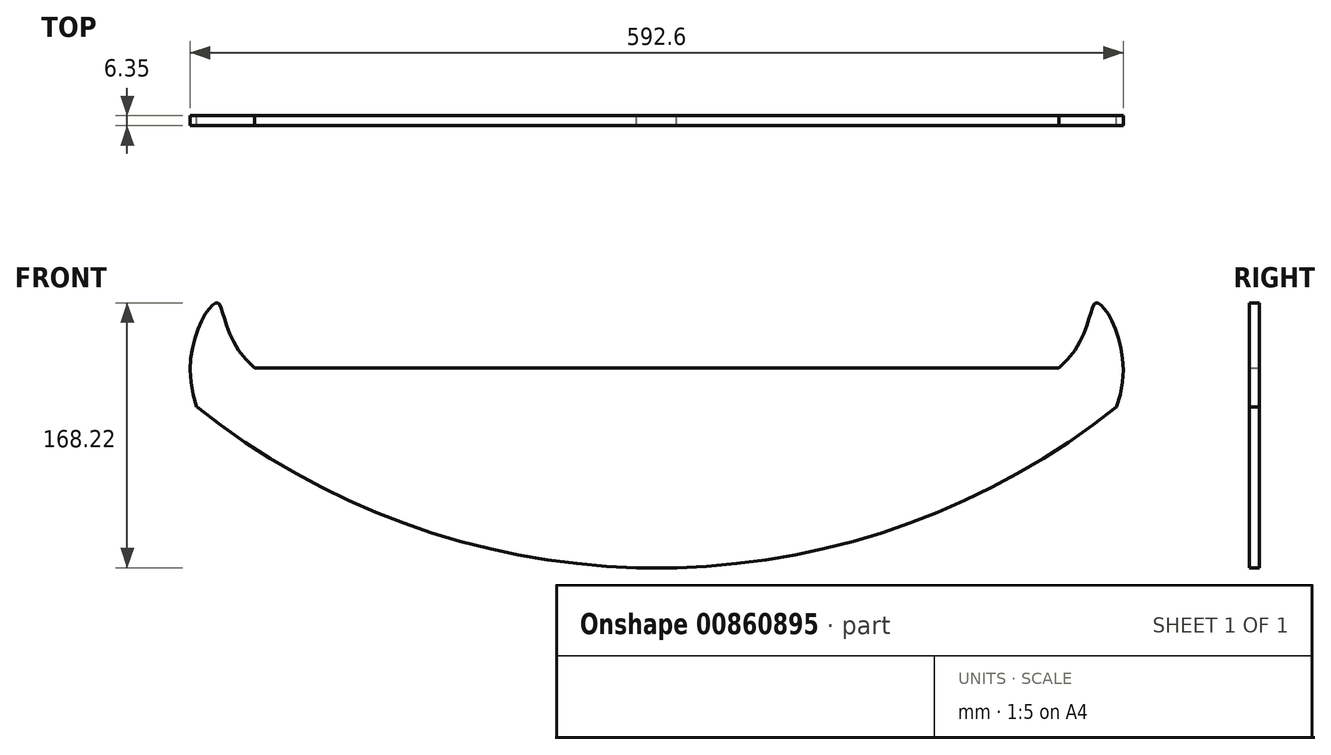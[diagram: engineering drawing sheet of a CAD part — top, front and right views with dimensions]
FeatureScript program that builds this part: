
annotation { "Feature Type Name" : "Feature", "Feature Type Description" : "" }
export const myFeature = defineFeature(function(context is Context, id is Id, definition is map)
    precondition{}
    {
        {
            var Q0;
            Q0=qCreatedBy(makeId("Front.planeOp"),FACE);
            var sketch = newSketch(context, id + "F0", { "sketchPlane" : qUnion([Q0])});
            skPoint(sketch, "E0.MirrorCS.start.orphan", {"position": v(292.1, -12) * mm});
            skPoint(sketch, "E1.MirrorCS.end.orphan", {"position": v(255.56, 12.77) * mm});
            skLineSegment(sketch, "E2", {"start": v(-255.56, 12.77) * mm, "end": v(-12.7, 12.77) * mm});
            skArc(sketch, "E3", {"start": v(-292.1, -12) * mm, "mid": v(-160.74, -85.92) * mm, "end": v(-12.7, -114.23) * mm});
            skFitSpline(sketch, "E4.MirrorCS", {"points": [v(292.1, -12) * mm, v(279.4, 53.98) * mm, v(255.56, 12.77) * mm], "startDerivative": vector(69.13, 182.58) * mm, "endDerivative": vector(-143.08, -126.29) * mm});
            skPoint(sketch, "E5.0.internal.orphan", {"position": v(-292.1, -12) * mm});
            skPoint(sketch, "E5.2.internal.orphan", {"position": v(-255.56, 12.77) * mm});
            skFitSpline(sketch, "E6.MirrorCS", {"points": [v(-292.1, -12) * mm, v(-279.4, 53.98) * mm, v(-255.56, 12.77) * mm], "startDerivative": vector(-69.13, 182.58) * mm, "endDerivative": vector(143.08, -126.29) * mm});
            skLineSegment(sketch, "E7.trimOffspring", {"start": v(12.7, 12.77) * mm, "end": v(255.56, 12.77) * mm});
            skArc(sketch, "E8.trimOffspring", {"start": v(12.7, -114.23) * mm, "mid": v(160.74, -85.92) * mm, "end": v(292.1, -12) * mm});
            skLineSegment(sketch, "E9", {"start": v(-12.7, 12.77) * mm, "end": v(12.7, 12.77) * mm});
            skLineSegment(sketch, "E10", {"start": v(-12.7, -114.23) * mm, "end": v(12.7, -114.23) * mm});
            skSolve(sketch);
        }
        {
            var Q0;
            Q0 = qSketchRegion(id + "F0", true);
            extrude(context, id + "F1", {"entities" : qUnion([Q0]), "depth" : 6.35 * mm, "offsetDistance" : 25.4 * mm});
        }
    });
